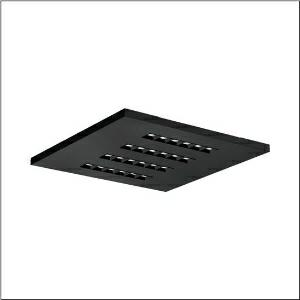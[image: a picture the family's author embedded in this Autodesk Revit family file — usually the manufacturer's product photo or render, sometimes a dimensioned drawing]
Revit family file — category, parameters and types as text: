
# Revit family: silica_r__21_square_51mx6kdu44b_e50d
name_source: partatom
category: Lighting Fixtures
units: mm (PartAtom-declared; Revit-internal decimal feet)

## family parameters
Cut with Voids When Loaded = No
Host = Face
Light Source = No
Part Type = Normal
Room Calculation Point = No
Round Connector Dimension = Use Diameter
Shared = No

## types (1)
- --- (1 x LED, 4600 lm, 29.6 W, 4000K)
    Apparent Load = 30 VA
    CIE Flux Codes = 86 100 100 100 100
    Color Rendering = 80
    Color Temperature = 4000K
    Default Elevation = 1800 mm
    Description = Silica® 21 Square, office luminaire, primary light control with lens, of PMMA, primary anti-glare with reflector, of PC, black, CAT 2 (L<= 3000cd/m²), light emission: direct distribution, primary light characteristic: symmetric, installation type: lay-in mounting, LED, rated luminous flux: 4.600lm, luminous efficacy: 155lm/W, light colour: 840, colour temperature: 4000K, control gear: DALI 2, with terminal, 5-pole, mains connection: 220..240V, AC, 50/60Hz, rated input power: 29.6W, luminaire housing, of aluminium, matt jet black (RAL 9005), module: M625, length: 622mm, width: 622mm, height: 33mm, protection rating (complete): IP20, insulation class (complete): insulation class I (protective earthing), certification: CE, ENEC, VDE, permissible operating ambient temperature: -20..+40°C, standard: EN 50419, packaging unit: 1 piece
    Height = 0 mm  [stored 0 ft]
    Lamp = 1 x LED
    Lamp Light Flux = 4600 lm
    Lamp Power = 29.6 W
    Lamp count = 1
    Length = 622 mm
    Luminous efficacy = 155 lm/W
    Manufacturer = Siteco
    ModVariant = No
    Model = 51MX6KDU44B
    Mounting Place = Ceiling
    Mounting Type = Recessed
    Number of Poles = 1
    OnlyDefault = Yes
    Power Factor = 1
    Product Name = Silica® 21 Square
    Product group = office luminaire | ceiling recessed
    ProductGroupID = 401
    Protection Class = Protection class I
    Protection Degree = IP 20
    RLX_Detail_Level = 1
    RLX_Emergency_Light_Flux = 0 lm
    RLX_Emergency_Type = 0
    RLX_Emergency_Type_DB = No
    RlxData = <blob elided: 25081 chars, md5=b46f5c62>
    Socket = socket
    Standby Power = 0 W
    System Light Flux = 4600 lm
    System Power = 30 W
    Type Comments = factory setting: luminous flux: 100 % | dim-lin: 254 | 399 mA
    Type Image = l_1275204.jpg
    URL = http://relux.com
    VarID = @adj_083866
    Voltage = 0 V
    Weight = 0.00 kg
    Width = 622 mm

note: [stored X ft] marks values corroborated as IEEE doubles in the binary element streams (Revit-internal decimal feet)

## geometry (parser evidence)
native form markers: Blend x4, Sweep x10
no freeform markers — native parametric forms only
